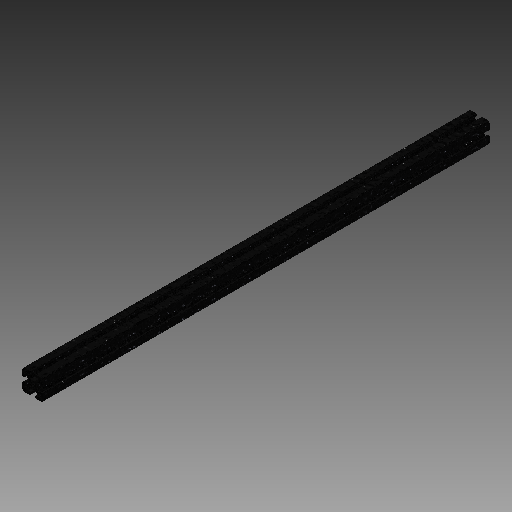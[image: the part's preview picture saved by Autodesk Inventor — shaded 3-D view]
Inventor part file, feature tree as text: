
AUTODESK INVENTOR PART (.ipt)
format: ipt  version: 2019 (Build 230136000, 136)  size: 250,368 bytes
history: native  units: in
note: dims shown in document units (in); Inventor stores cm internally (conversion verified against a paired STEP export)
features: plane x1, extrude x1, sketch x1
ambient origin geometry x8: Origin, YZ Plane, XZ Plane, XY Plane, X Axis, Y Axis, Z Axis, Center Point
bodies: Solid1 (feature_tree)
feature tree (3):
  plane  "Work Plane1"
  extrude  "Extrusion1"  [1 undecoded]
  sketch  "Sketch1"  dims[d0=32.5in d1=0.0in]
note: 1 required parameter value undecoded (feature->parameter linkage not recoverable at this tier; creation-order binding heuristic only, values carry confidence <= 0.55)
